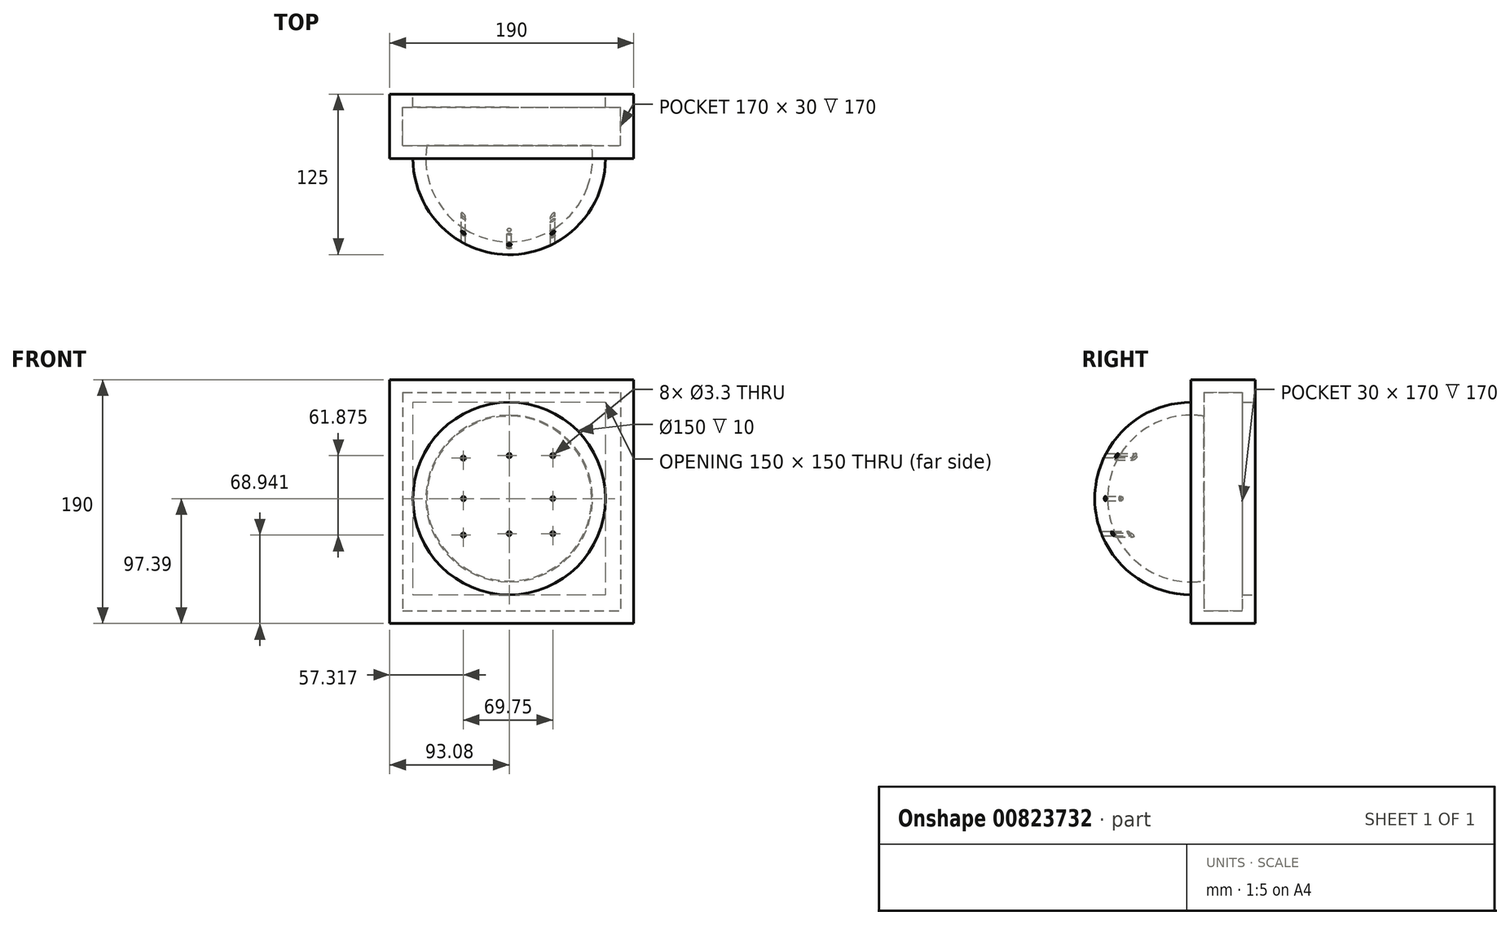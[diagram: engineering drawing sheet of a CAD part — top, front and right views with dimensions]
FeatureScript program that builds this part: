
annotation { "Feature Type Name" : "Feature", "Feature Type Description" : "" }
export const myFeature = defineFeature(function(context is Context, id is Id, definition is map)
    precondition{}
    {
        {
            var Q0;
            Q0=qCreatedBy(makeId("Front.planeOp"),FACE);
            var sketch = newSketch(context, id + "F0", { "sketchPlane" : qUnion([Q0])});
            skLineSegment(sketch, "E0.bottom", {"start": v(-93.08, 92.61) * mm, "end": v(96.92, 92.61) * mm});
            skLineSegment(sketch, "E0.top", {"start": v(-93.08, -97.39) * mm, "end": v(96.92, -97.39) * mm});
            skLineSegment(sketch, "E0.left", {"start": v(-93.08, 92.61) * mm, "end": v(-93.08, -97.39) * mm});
            skLineSegment(sketch, "E0.right", {"start": v(96.92, 92.61) * mm, "end": v(96.92, -97.39) * mm});
            skSolve(sketch);
        }
        {
            var Q0;
            Q0 = qSketchRegion(id + "F0", true);
            extrude(context, id + "F1", {"entities" : qUnion([Q0]), "depth" : 50 * mm, "offsetDistance" : 25 * mm});
        }
        {
            var Q0;
            Q0=makeQuery(id+"F1.opExtrude","CAP_FACE",FACE,{"disambiguationData":[OSD([sQuery(id+"F0.wireOp",EDGE,"E0.bottom"),sQuery(id+"F0.wireOp",EDGE,"E0.top"),sQuery(id+"F0.wireOp",EDGE,"E0.left"),sQuery(id+"F0.wireOp",EDGE,"E0.right")])],"isStart":false});
            var sketch = newSketch(context, id + "F2", { "sketchPlane" : qUnion([Q0])});
            skArc(sketch, "E1", {"start": v(0, 75) * mm, "mid": v(-75, 0) * mm, "end": v(0, -75) * mm});
            skLineSegment(sketch, "E2", {"start": v(0, 75) * mm, "end": v(0, -75) * mm});
            skSolve(sketch);
        }
        {
            var Q0;
            Q0=makeQuery(id+"F2.imprint","IMPRINT",FACE,{"disambiguationData":[TD([[makeQuery(id+"F2.imprint","IMPRINT",EDGE,{"derivedFrom":sQuery(id+"F2.wireOp",EDGE,"E1")}),1.0]])]});
            var Q1;
            Q1=sQuery(id+"F2.wireOp",EDGE,"E2");
            revolve(context, id + "F3", {"operationType" : NewBodyOperationType.ADD, "surfaceOperationType" : NewSurfaceOperationType.NEW, "entities" : qUnion([Q0]), "axis" : qUnion([Q1]), "revolveType" : RevolveType.ONE_DIRECTION, "oppositeDirection" : true, "angle" : 180 * degree});
        }
        {
            var Q0;
            Q0=makeQuery(id+"F3.opRevolve","SWEPT_FACE",FACE,{"disambiguationData":[OSD([sQuery(id+"F2.wireOp",EDGE,"E1")])]});
            var Q1;
            Q1=makeQuery(id+"F1.opExtrude","SWEPT_BODY",BODY,{"disambiguationData":[OSD([sQuery(id+"F0.wireOp",EDGE,"E0.bottom"),sQuery(id+"F0.wireOp",EDGE,"E0.top"),sQuery(id+"F0.wireOp",EDGE,"E0.left"),sQuery(id+"F0.wireOp",EDGE,"E0.right")])]});
            shell(context, id + "F4", {"isHollow" : true, "entities" : qUnion([Q0]), "parts" : qUnion([Q1]), "thickness" : 10 * mm});
        }
        {
            var Q0;
            Q0=makeQuery(id+"F1.opExtrude","CAP_FACE",FACE,{"disambiguationData":[OSD([sQuery(id+"F0.wireOp",EDGE,"E0.bottom"),sQuery(id+"F0.wireOp",EDGE,"E0.top"),sQuery(id+"F0.wireOp",EDGE,"E0.left"),sQuery(id+"F0.wireOp",EDGE,"E0.right")])],"isStart":true});
            var sketch = newSketch(context, id + "F5", { "sketchPlane" : qUnion([Q0])});
            skCircle(sketch, "E3", {"center": v(0, 0) * mm, "radius": 75 * mm});
            skSolve(sketch);
        }
        {
            var Q0;
            Q0 = qSketchRegion(id + "F5", true);
            extrude(context, id + "F6", {"entities" : qUnion([Q0]), "operationType" : NewBodyOperationType.REMOVE, "oppositeDirection" : true, "depth" : 25 * mm, "offsetDistance" : 25 * mm});
        }
        {
            var Q0;
            Q0=makeQuery(id+"F1.opExtrude","CAP_FACE",FACE,{"disambiguationData":[OSD([sQuery(id+"F0.wireOp",EDGE,"E0.bottom"),sQuery(id+"F0.wireOp",EDGE,"E0.top"),sQuery(id+"F0.wireOp",EDGE,"E0.left"),sQuery(id+"F0.wireOp",EDGE,"E0.right")])],"isStart":false});
            var sketch = newSketch(context, id + "F7", { "sketchPlane" : qUnion([Q0])});
            skPoint(sketch, "E4", {"position": v(-35.76, 31.55) * mm});
            skPoint(sketch, "E5", {"position": v(0, 33.43) * mm});
            skPoint(sketch, "E6", {"position": v(33.99, 33.43) * mm});
            skPoint(sketch, "E7", {"position": v(33.99, 0) * mm});
            skPoint(sketch, "E8", {"position": v(33.99, -27.32) * mm});
            skPoint(sketch, "E9", {"position": v(0, -27.32) * mm});
            skPoint(sketch, "E10", {"position": v(-35.76, 0) * mm});
            skPoint(sketch, "E11", {"position": v(-35.76, -28.45) * mm});
            skSolve(sketch);
        }
        {
            var Q0;
            Q0=sQuery(id+"F7.wireOp",VERTEX,"E4");
            var Q1;
            Q1=sQuery(id+"F7.wireOp",VERTEX,"E5");
            var Q2;
            Q2=sQuery(id+"F7.wireOp",VERTEX,"E6");
            var Q3;
            Q3=sQuery(id+"F7.wireOp",VERTEX,"E7");
            var Q4;
            Q4=sQuery(id+"F7.wireOp",VERTEX,"E8");
            var Q5;
            Q5=sQuery(id+"F7.wireOp",VERTEX,"E9");
            var Q6;
            Q6=sQuery(id+"F7.wireOp",VERTEX,"E11");
            var Q7;
            Q7=sQuery(id+"F7.wireOp",VERTEX,"E10");
            var Q8;
            Q8=makeQuery(id+"F1.opExtrude","SWEPT_BODY",BODY,{"disambiguationData":[OSD([sQuery(id+"F0.wireOp",EDGE,"E0.bottom"),sQuery(id+"F0.wireOp",EDGE,"E0.top"),sQuery(id+"F0.wireOp",EDGE,"E0.left"),sQuery(id+"F0.wireOp",EDGE,"E0.right")])]});
            hole(context, id + "F8", {"style" : HoleStyle.C_BORE, "endStyle" : HoleEndStyle.THROUGH, "oppositeDirection" : true, "holeDiameter" : 3.3 * mm, "cBoreDiameter" : 6.5 * mm, "cBoreDepth" : 3 * mm, "majorDiameter" : 5 * mm, "isTappedThrough" : true, "tappedDepth" : 12 * mm, "tapClearance" : 3, "startFromSketch" : true, "locations" : qUnion([Q0, Q1, Q2, Q3, Q4, Q5, Q6, Q7]), "scope" : qUnion([Q8])});
        }
    });
